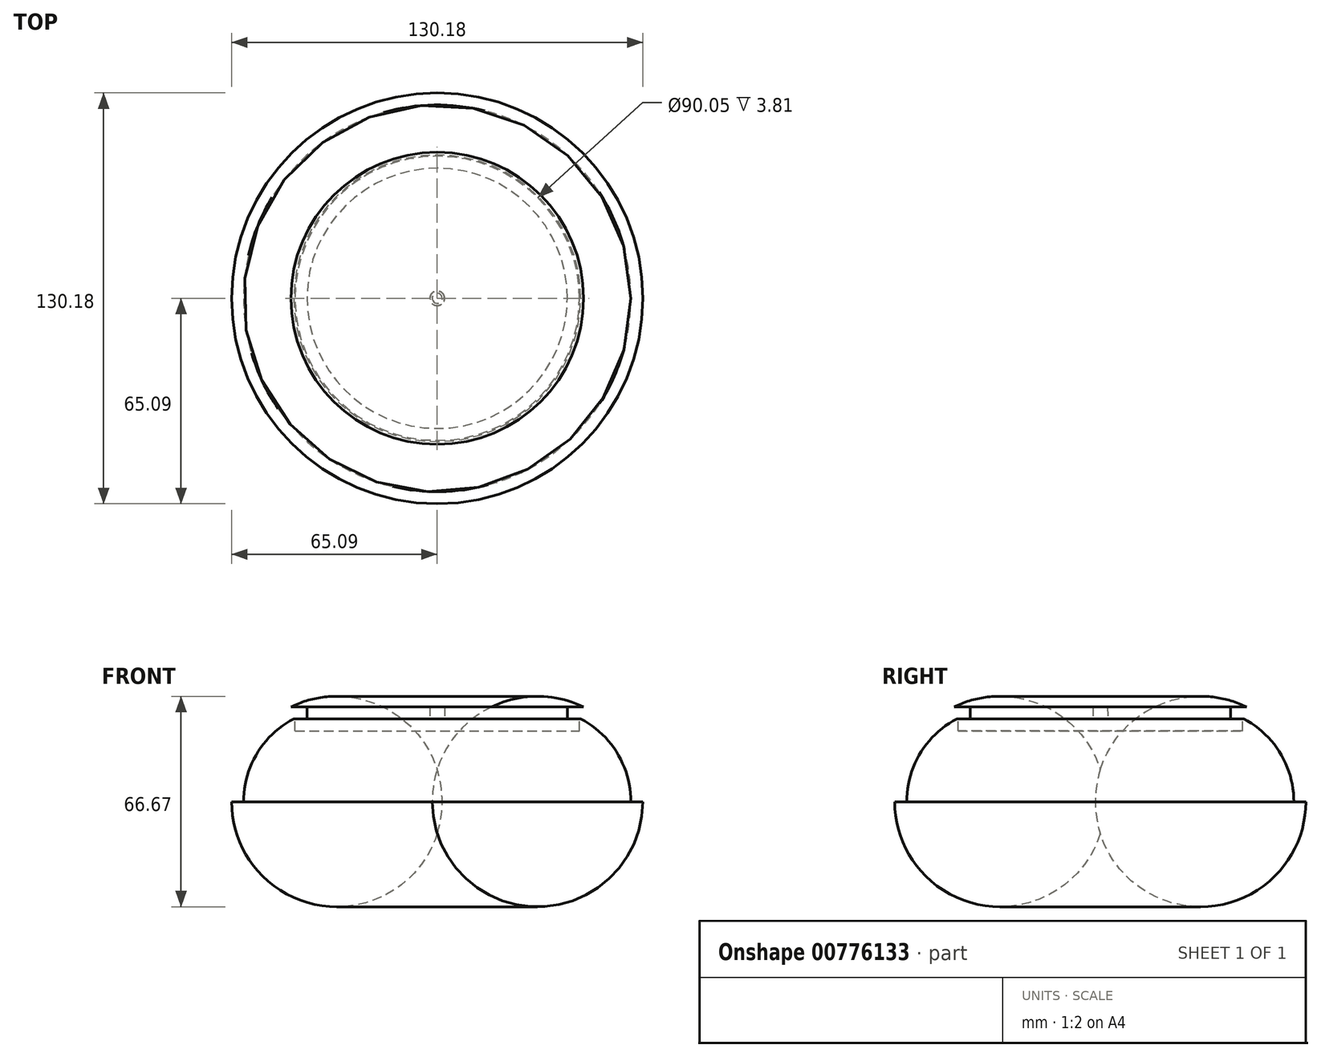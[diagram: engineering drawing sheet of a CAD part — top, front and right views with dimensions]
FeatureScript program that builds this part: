
annotation { "Feature Type Name" : "Feature", "Feature Type Description" : "" }
export const myFeature = defineFeature(function(context is Context, id is Id, definition is map)
    precondition{}
    {
        {
            var Q0;
            Q0=qCreatedBy(makeId("Right.planeOp"),FACE);
            var sketch = newSketch(context, id + "F0", { "sketchPlane" : qUnion([Q0])});
            skLineSegment(sketch, "E0", {"start": v(-63.5, 0) * mm, "end": v(63.5, 0) * mm});
            skLineSegment(sketch, "E1", {"start": v(-46.3, 30.16) * mm, "end": v(-46.3, 0) * mm});
            skLineSegment(sketch, "E2", {"start": v(-27.32, 53.98) * mm, "end": v(-27.32, 0) * mm});
            skLineSegment(sketch, "E3", {"start": v(0, 76.2) * mm, "end": v(0, 0) * mm});
            skLineSegment(sketch, "E4", {"start": v(18.77, 101.6) * mm, "end": v(18.77, 0) * mm});
            skSolve(sketch);
        }
        {
            var Q0;
            Q0=qCreatedBy(makeId("Right.planeOp"),FACE);
            var sketch = newSketch(context, id + "F1", { "sketchPlane" : qUnion([Q0])});
            skLineSegment(sketch, "E5", {"start": v(0, 30.16) * mm, "end": v(-46.3, 30.16) * mm, "construction": true});
            skLineSegment(sketch, "E6", {"start": v(0, 30.16) * mm, "end": v(0, 0) * mm, "construction": true});
            skLineSegment(sketch, "E7", {"start": v(0, 0) * mm, "end": v(-65.09, 0) * mm});
            skArc(sketch, "E8", {"start": v(-46.3, 30.16) * mm, "mid": v(-60.05, 17.8) * mm, "end": v(-65.09, 0) * mm});
            skLineSegment(sketch, "E9", {"start": v(-46.3, 30.16) * mm, "end": v(-41.22, 30.16) * mm});
            skLineSegment(sketch, "E10", {"start": v(-41.22, 30.16) * mm, "end": v(-41.22, 26.35) * mm});
            skLineSegment(sketch, "E11", {"start": v(0, 30.16) * mm, "end": v(0, 0) * mm});
            skLineSegment(sketch, "E12", {"start": v(-41.22, 26.35) * mm, "end": v(-2.35, 26.35) * mm});
            skLineSegment(sketch, "E13", {"start": v(-2.29, 30.16) * mm, "end": v(0, 30.16) * mm});
            skLineSegment(sketch, "E14", {"start": v(-2.29, 30.16) * mm, "end": v(-2.35, 26.35) * mm});
            skSolve(sketch);
        }
        {
            var Q0;
            Q0=makeQuery(id+"F1.imprint","IMPRINT",FACE,{"disambiguationData":[TD([[makeQuery(id+"F1.imprint","IMPRINT",EDGE,{"derivedFrom":sQuery(id+"F1.wireOp",EDGE,"E7")}),-1.0]])]});
            var Q1;
            Q1=sQuery(id+"F1.wireOp",EDGE,"E6");
            revolve(context, id + "F2", {"surfaceOperationType" : NewSurfaceOperationType.NEW, "entities" : qUnion([Q0]), "axis" : qUnion([Q1]), "revolveType" : RevolveType.FULL});
        }
        {
            var Q0;
            Q0=makeQuery(id+"F2.opRevolve","SWEPT_FACE",FACE,{"disambiguationData":[OSD([sQuery(id+"F1.wireOp",EDGE,"E7")])]});
            shell(context, id + "F3", {"entities" : qUnion([Q0]), "thickness" : 3.8 * mm});
        }
    });
